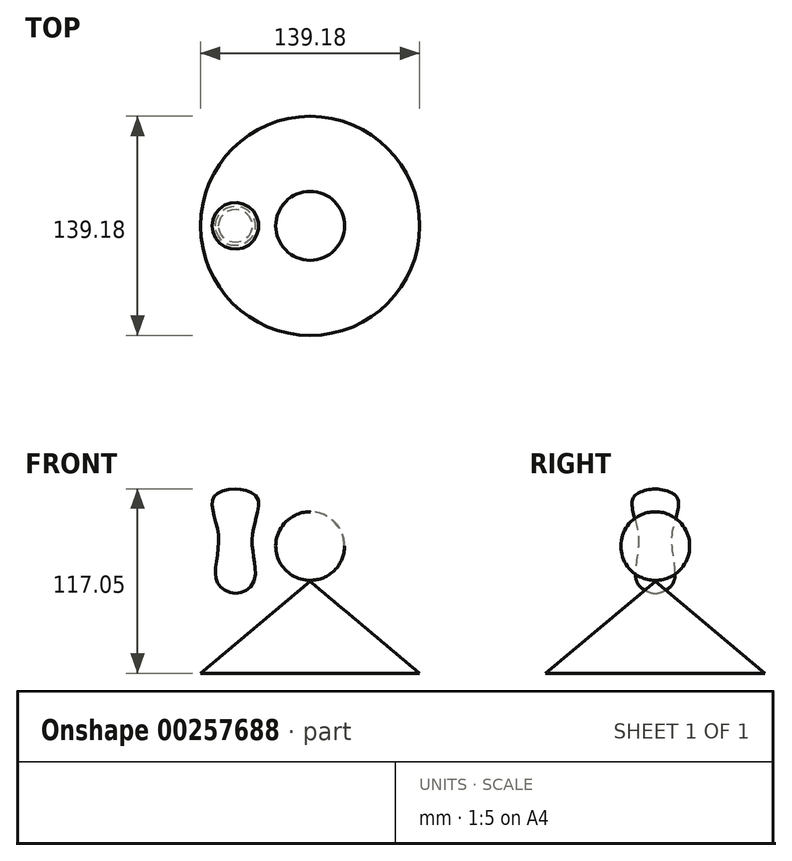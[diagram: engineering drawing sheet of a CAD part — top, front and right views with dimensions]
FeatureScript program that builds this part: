
annotation { "Feature Type Name" : "Feature", "Feature Type Description" : "" }
export const myFeature = defineFeature(function(context is Context, id is Id, definition is map)
    precondition{}
    {
        {
            var Q0;
            Q0=qCreatedBy(makeId("Top.planeOp"),FACE);
            var sketch = newSketch(context, id + "F0", { "sketchPlane" : qUnion([Q0])});
            skCircle(sketch, "E0", {"center": v(0, 0) * mm, "radius": 10 * mm});
            skSolve(sketch);
        }
        {
            var Q0;
            Q0=makeQuery(id+"F0.imprint","IMPRINT",FACE,{"disambiguationData":[TD([[makeQuery(id+"F0.imprint","IMPRINT",EDGE,{"derivedFrom":sQuery(id+"F0.wireOp",EDGE,"E0")}),1.0]])]});
            extrude(context, id + "F1", {"entities" : qUnion([Q0]), "depth" : 50 * mm, "hasDraft" : true, "draftAngle" : 50 * degree, "draftPullDirection" : true, "hasSecondDirection" : true, "secondDirectionOppositeDirection" : true, "secondDirectionDepth" : 50 * mm, "hasSecondDirectionDraft" : true, "secondDirectionDraftAngle" : 50 * degree});
        }
        {
            var Q0;
            Q0=qCreatedBy(makeId("Front.planeOp"),FACE);
            var sketch = newSketch(context, id + "F2", { "sketchPlane" : qUnion([Q0])});
            skArc(sketch, "E1", {"start": v(0, 52.54) * mm, "mid": v(-21.88, 30.76) * mm, "end": v(0, 8.99) * mm});
            skLineSegment(sketch, "E2", {"start": v(0, 55.32) * mm, "end": v(0, 8.99) * mm});
            skSolve(sketch);
        }
        {
            var Q0;
            {var subQ0=sQuery(id+"F2.wireOp",EDGE,"E1");Q0=makeQuery(id+"F2.imprint","IMPRINT",FACE,{"disambiguationData":[TD([[makeQuery(id+"F2.imprint","IMPRINT",EDGE,{"derivedFrom":subQ0}),1.0]])]});}
            var Q1;
            Q1=sQuery(id+"F2.wireOp",EDGE,"E2");
            revolve(context, id + "F3", {"entities" : qUnion([Q0]), "axis" : qUnion([Q1]), "revolveType" : RevolveType.FULL});
        }
        {
            var Q0;
            Q0=qCreatedBy(makeId("Front.planeOp"),FACE);
            var sketch = newSketch(context, id + "F4", { "sketchPlane" : qUnion([Q0])});
            skFitSpline(sketch, "E3", {"points": [v(-58.18, 36.65) * mm, v(-58.18, 6.2) * mm, v(-37.27, 2.78) * mm, v(-31.58, 40.28) * mm, v(-31.81, 63.7) * mm, v(-60.45, 62.78) * mm, v(-58.18, 36.65) * mm]});
            skLineSegment(sketch, "E4", {"start": v(-47.5, 70.97) * mm, "end": v(-47.5, -4.72) * mm});
            skSolve(sketch);
        }
        {
            var Q0;
            {var subQ0=sQuery(id+"F4.wireOp",EDGE,"E4");var subQ1=sQuery(id+"F4.wireOp",EDGE,"E3");var subQ2=makeQuery(id+"F4.imprint","INTERSECT",VERTEX,{"disambiguationData":[OD(0.0)],"derivedFrom":[subQ1,subQ0]});Q0=makeQuery(id+"F4.imprint","IMPRINT",FACE,{"disambiguationData":[TD([[makeQuery(id+"F4.imprint","IMPRINT",EDGE,{"disambiguationData":[TD([[subQ2,1.0]])],"derivedFrom":subQ1}),1.0]])]});}
            var Q1;
            Q1=sQuery(id+"F4.wireOp",EDGE,"E4");
            revolve(context, id + "F5", {"entities" : qUnion([Q0]), "axis" : qUnion([Q1]), "revolveType" : RevolveType.FULL});
        }
    });
